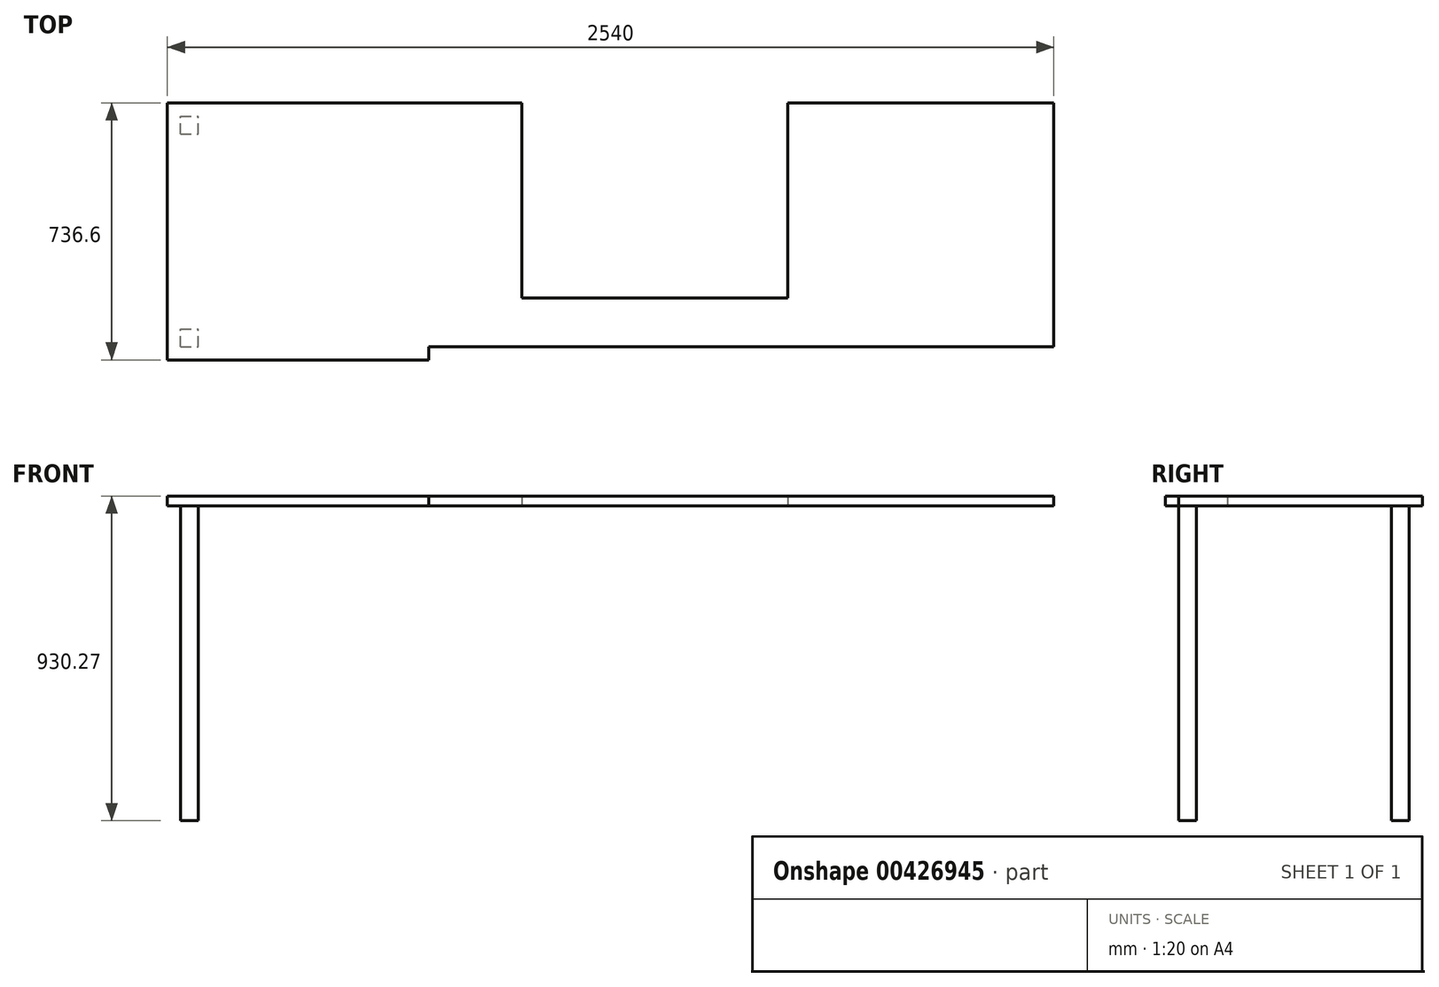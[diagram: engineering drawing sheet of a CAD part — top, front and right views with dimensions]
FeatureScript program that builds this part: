
annotation { "Feature Type Name" : "Feature", "Feature Type Description" : "" }
export const myFeature = defineFeature(function(context is Context, id is Id, definition is map)
    precondition{}
    {
        {
            var Q0;
            Q0=qCreatedBy(makeId("Top.planeOp"),FACE);
            var sketch = newSketch(context, id + "F0", { "sketchPlane" : qUnion([Q0])});
            skLineSegment(sketch, "E0", {"start": v(0, 0) * mm, "end": v(0, 698.5) * mm});
            skLineSegment(sketch, "E1", {"start": v(0, 698.5) * mm, "end": v(-762, 698.5) * mm});
            skLineSegment(sketch, "E2", {"start": v(-762, 698.5) * mm, "end": v(-762, 139.7) * mm});
            skLineSegment(sketch, "E3", {"start": v(-762, 139.7) * mm, "end": v(-1524, 139.7) * mm});
            skLineSegment(sketch, "E4", {"start": v(-1524, 139.7) * mm, "end": v(-1524, 698.5) * mm});
            skLineSegment(sketch, "E5", {"start": v(-1524, 698.5) * mm, "end": v(-2540, 698.5) * mm});
            skLineSegment(sketch, "E6", {"start": v(-2540, 698.5) * mm, "end": v(-2540, 0) * mm});
            skLineSegment(sketch, "E7", {"start": v(0, 0) * mm, "end": v(-1790.7, 0) * mm});
            skLineSegment(sketch, "E8", {"start": v(-1790.7, 0) * mm, "end": v(-1790.7, -38.1) * mm});
            skLineSegment(sketch, "E9", {"start": v(-1790.7, -38.1) * mm, "end": v(-2540, -38.1) * mm});
            skLineSegment(sketch, "E10", {"start": v(-2540, -38.1) * mm, "end": v(-2540, 0) * mm});
            skSolve(sketch);
        }
        {
            var Q0;
            Q0=makeQuery(id+"F0.imprint","IMPRINT",FACE,{"disambiguationData":[TD([[makeQuery(id+"F0.imprint","IMPRINT",EDGE,{"derivedFrom":sQuery(id+"F0.wireOp",EDGE,"E0")}),1.0]])]});
            extrude(context, id + "F1", {"entities" : qUnion([Q0]), "depth" : 28.57 * mm});
        }
        {
            var Q0;
            Q0=makeQuery(id+"F1.opExtrude","CAP_FACE",FACE,{"disambiguationData":[OSD([sQuery(id+"F0.wireOp",EDGE,"E0"),sQuery(id+"F0.wireOp",EDGE,"E1"),sQuery(id+"F0.wireOp",EDGE,"E2"),sQuery(id+"F0.wireOp",EDGE,"E3"),sQuery(id+"F0.wireOp",EDGE,"E4"),sQuery(id+"F0.wireOp",EDGE,"E5"),sQuery(id+"F0.wireOp",EDGE,"E6"),sQuery(id+"F0.wireOp",EDGE,"E7"),sQuery(id+"F0.wireOp",EDGE,"E8"),sQuery(id+"F0.wireOp",EDGE,"E9"),sQuery(id+"F0.wireOp",EDGE,"E10")])],"isStart":true});
            var sketch = newSketch(context, id + "F2", { "sketchPlane" : qUnion([Q0])});
            skLineSegment(sketch, "E11.bottom", {"start": v(-2501.9, 0) * mm, "end": v(-2451.1, 0) * mm});
            skLineSegment(sketch, "E11.top", {"start": v(-2501.9, -50.8) * mm, "end": v(-2451.1, -50.8) * mm});
            skLineSegment(sketch, "E11.left", {"start": v(-2501.9, 0) * mm, "end": v(-2501.9, -50.8) * mm});
            skLineSegment(sketch, "E11.right", {"start": v(-2451.1, 0) * mm, "end": v(-2451.1, -50.8) * mm});
            skLineSegment(sketch, "E12.bottom", {"start": v(-2501.9, -609.6) * mm, "end": v(-2451.1, -609.6) * mm});
            skLineSegment(sketch, "E12.top", {"start": v(-2501.9, -660.4) * mm, "end": v(-2451.1, -660.4) * mm});
            skLineSegment(sketch, "E12.left", {"start": v(-2501.9, -609.6) * mm, "end": v(-2501.9, -660.4) * mm});
            skLineSegment(sketch, "E12.right", {"start": v(-2451.1, -609.6) * mm, "end": v(-2451.1, -660.4) * mm});
            skSolve(sketch);
        }
        {
            var Q0;
            Q0=makeQuery(id+"F2.imprint","IMPRINT",FACE,{"disambiguationData":[TD([[makeQuery(id+"F2.imprint","IMPRINT",EDGE,{"derivedFrom":sQuery(id+"F2.wireOp",EDGE,"E11.bottom")}),-1.0]])]});
            var Q1;
            Q1=makeQuery(id+"F2.imprint","IMPRINT",FACE,{"disambiguationData":[TD([[makeQuery(id+"F2.imprint","IMPRINT",EDGE,{"derivedFrom":sQuery(id+"F2.wireOp",EDGE,"E12.bottom")}),-1.0]])]});
            extrude(context, id + "F3", {"entities" : qUnion([Q0, Q1]), "operationType" : NewBodyOperationType.ADD, "depth" : 901.7 * mm});
        }
    });
